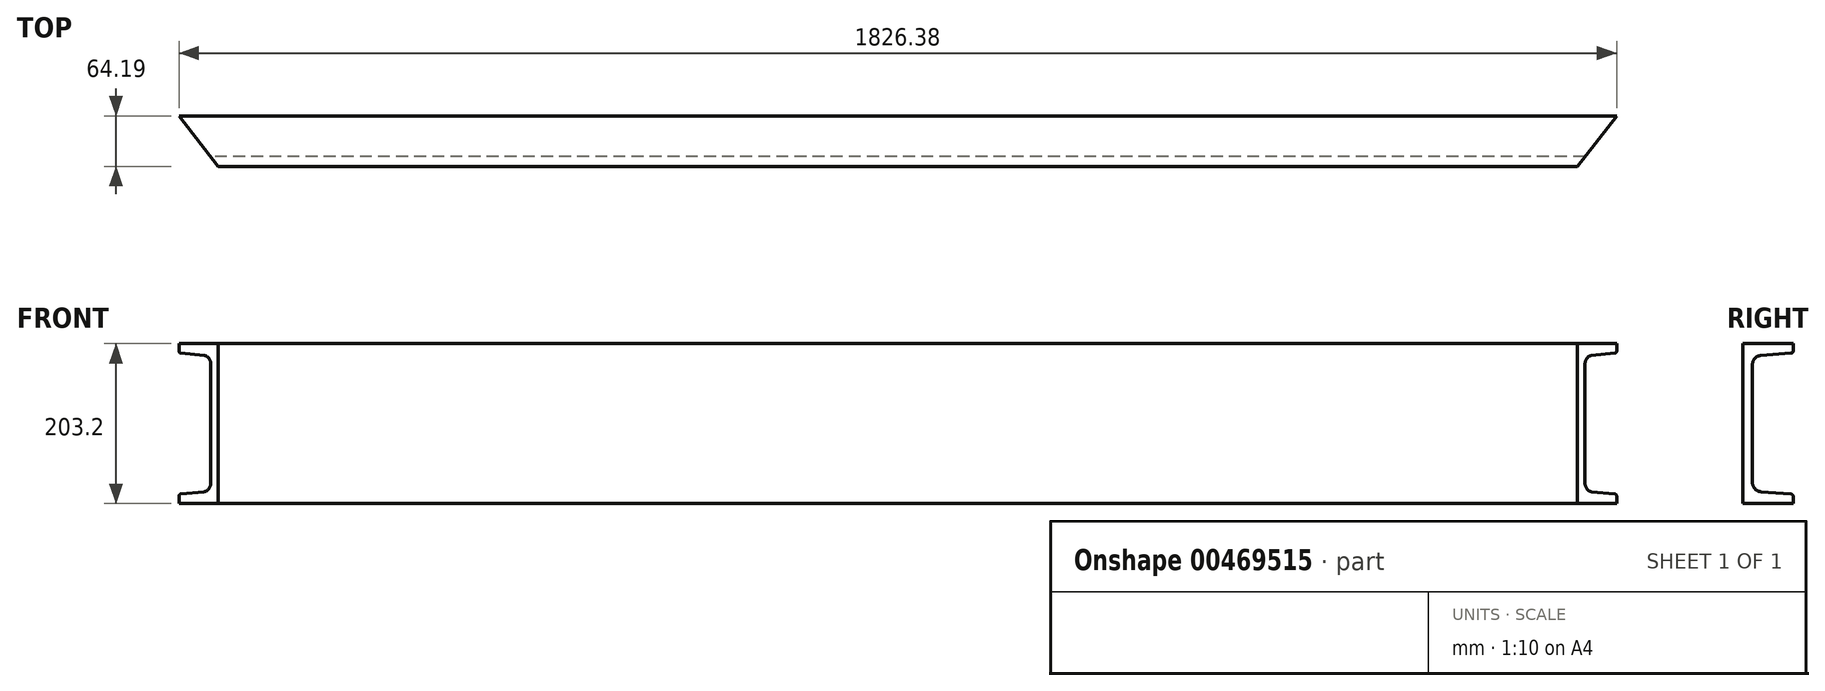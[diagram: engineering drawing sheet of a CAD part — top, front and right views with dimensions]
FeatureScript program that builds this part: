
annotation { "Feature Type Name" : "Feature", "Feature Type Description" : "" }
export const myFeature = defineFeature(function(context is Context, id is Id, definition is map)
    precondition{}
    {
        {
            var Q0;
            Q0=qCreatedBy(makeId("Right.planeOp"),FACE);
            var sketch = newSketch(context, id + "F0", { "sketchPlane" : qUnion([Q0])});
            skLineSegment(sketch, "E0", {"start": v(0, 101.6) * mm, "end": v(0, -101.6) * mm});
            skLineSegment(sketch, "E1", {"start": v(0, -101.6) * mm, "end": v(64.19, -101.6) * mm});
            skLineSegment(sketch, "E2", {"start": v(64.19, -101.6) * mm, "end": v(64.19, -92.64) * mm});
            skLineSegment(sketch, "E3", {"start": v(61.25, -89.47) * mm, "end": v(23.16, -86.57) * mm});
            skLineSegment(sketch, "E4", {"start": v(12.37, -74.93) * mm, "end": v(12.37, 74.93) * mm});
            skLineSegment(sketch, "E5", {"start": v(23.16, 86.57) * mm, "end": v(61.25, 89.47) * mm});
            skLineSegment(sketch, "E6", {"start": v(64.19, 92.64) * mm, "end": v(64.19, 101.6) * mm});
            skLineSegment(sketch, "E7", {"start": v(64.19, 101.6) * mm, "end": v(0, 101.6) * mm});
            skPoint(sketch, "E8.visualSharp", {"position": v(64.19, 89.7) * mm});
            skArc(sketch, "E8.filletArc", {"start": v(61.25, 89.47) * mm, "mid": v(63.34, 90.48) * mm, "end": v(64.19, 92.64) * mm});
            skPoint(sketch, "E9.visualSharp", {"position": v(64.19, -89.7) * mm});
            skArc(sketch, "E9.filletArc", {"start": v(64.19, -92.64) * mm, "mid": v(63.34, -90.48) * mm, "end": v(61.25, -89.47) * mm});
            skPoint(sketch, "E10.visualSharp", {"position": v(12.37, -85.75) * mm});
            skArc(sketch, "E10.filletArc", {"start": v(12.37, -74.93) * mm, "mid": v(15.48, -82.87) * mm, "end": v(23.16, -86.57) * mm});
            skPoint(sketch, "E11.visualSharp", {"position": v(12.37, 85.75) * mm});
            skArc(sketch, "E11.filletArc", {"start": v(23.16, 86.57) * mm, "mid": v(15.48, 82.87) * mm, "end": v(12.37, 74.93) * mm});
            skSolve(sketch);
        }
        {
            var Q0;
            Q0 = qSketchRegion(id + "F0", true);
            extrude(context, id + "F1", {"entities" : qUnion([Q0]), "endBound" : BoundingType.SYMMETRIC, "depth" : 1854.2 * mm});
        }
        {
            var Q0;
            Q0=makeQuery(id+"F1.opExtrude","SWEPT_FACE",FACE,{"disambiguationData":[OSD([sQuery(id+"F0.wireOp",EDGE,"E7")])]});
            var sketch = newSketch(context, id + "F2", { "sketchPlane" : qUnion([Q0])});
            skLineSegment(sketch, "E12", {"start": v(-927.1, 64.19) * mm, "end": v(-927.1, 0) * mm});
            skLineSegment(sketch, "E13", {"start": v(-927.1, 0) * mm, "end": v(-863.13, 0) * mm});
            skLineSegment(sketch, "E14", {"start": v(-863.13, 0) * mm, "end": v(-913.19, 64.19) * mm});
            skLineSegment(sketch, "E15", {"start": v(-913.19, 64.19) * mm, "end": v(-927.1, 64.19) * mm});
            skLineSegment(sketch, "E16", {"start": v(927.1, 64.19) * mm, "end": v(913.19, 64.19) * mm});
            skLineSegment(sketch, "E17", {"start": v(913.19, 64.19) * mm, "end": v(863.13, 0) * mm});
            skLineSegment(sketch, "E18", {"start": v(863.13, 0) * mm, "end": v(927.1, 0) * mm});
            skLineSegment(sketch, "E19", {"start": v(927.1, 0) * mm, "end": v(927.1, 64.19) * mm});
            skSolve(sketch);
        }
        {
            var Q0;
            Q0 = qSketchRegion(id + "F2", true);
            extrude(context, id + "F3", {"entities" : qUnion([Q0]), "operationType" : NewBodyOperationType.REMOVE, "endBound" : BoundingType.THROUGH_ALL, "oppositeDirection" : true, "depth" : 25.4 * mm});
        }
    });
